# Revit family: Hager-Orion_Plus-IP65-D160-Cl.I-Steel_encl-630A-NoHosted-FR-fr
name_source: partatom
category: Equipement électrique
units: mm (PartAtom-declared; Revit-internal decimal feet)

## family parameters
Basée sur le plan de construction = Oui
Configuration du panneau = Deux colonnes, circuits au sein
Cote de connecteur circulaire = Utiliser le diamètre
Couper avec des vides une fois chargée = Non
Partagée = Non
Point de calcul de pièce = Non
Toujours verticalement = Oui
Type d'élément = Tableau de raccordement

## types (3) — shared parameters
Commentaires du type = Orion Plus
EF000003 - mode de pose = EV000384 - saillie
EF000007 - couleur = EV000270 - gris
EF000049 - profondeur = 160 mm  [stored 0.524934 ft]
EF000116 - numéro RAL = 7035
EF000118 - avec cadre/support de montage = Non
EF000437 - nombre d'entrées de conduit = 2
EF001088 - possibilité de montage en saillie = Oui
EF001131 - profondeur intérieure = 160 mm  [stored 0.524934 ft]
EF001596 - matériau du boîtier/corps = EV000179 - acier
EF001613 - maintien de fonction = EV000494 - sans
EF003532 - convient pour utilisation à l’extérieur = Non
EF004293 - indice de protection contre les chocs (IK) = EV008784 - IK10
EF004464 - type de porte = EV002646 - unique
EF005474 - indice de protection (IP) = EV006421 - IP65
EF006306 - avec serrure = Oui
EF007800 - adapté à un parafoudre = Non
EF008873 - courant nominal (In) = 630 A
EF009171 - épaisseur de matériau de la porte/du couvercle = 2 mm  [stored 0.00656168 ft]
EF009554 - nombre d'ouvertures pour plaques à bride = 2
EF015940 - couvercle avec décharge de pression = Non
Elévation par défaut = 1219 mm
Fabricant = Hager
HG000002 - avec porte = Oui
HG000003 - Gamme = Orion Plus
HG000006 - Encastré = Non
HG000009 - Porte à double battant = Non
HG000010 - Portes asymétriques = Non
HG000023 - Armoire double section = Non
HG000024 - Hauteur de la section basse = 600 mm
HG000026 - Installation au sol = Non
zero-valued in all types: EF000218 - profondeur d'encastrement, HG000027 - Hauteur du socle

## per-type parameters (varying)
| type | EF000008 - largeur | EF000040 - hauteur | EF000266 - nombre de rangées | EF000339 - type de capot | EF002950 - largeur en nombre de modules | EF004427 - nombre de modules | EF006244 - couvercle/porte transparent(e) | EF009170 - épaisseur de matériau du boîtier | EF009212 - finition du couvercle | HG000004 - Référence fabricant |
| saillie IP65 L250 H300 P160  - FL102A | 250 mm  [stored 0.82021 ft] | 300 mm | 1 | EV004216 - porte | 0 | 0 | Non | 2 mm  [stored 0.00656168 ft] | EV009916 - avec échancrure | FL102A |
| saillie IP65 L300 H350 P160  - FL104A | 300 mm | 350 mm  [stored 1.14829 ft] | 2 | EV001012 - couvercle | 10 | 20 | Non | 2 mm  [stored 0.00656168 ft] | EV000116 - fermé | FL104A |
| saillie IP65 L300 H350 P160  - FL154A | 300 mm | 350 mm  [stored 1.14829 ft] | 2 | EV004216 - porte | 10 | 20 | Oui | 1 mm  [stored 0.00328084 ft] | EV000116 - fermé | FL154A |

note: [stored X ft] marks values corroborated as IEEE doubles in the binary element streams (Revit-internal decimal feet)

## geometry (parser evidence)
native form markers: Blend x4, Sweep x10
no freeform markers — native parametric forms only
